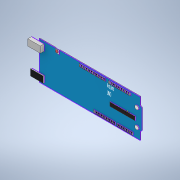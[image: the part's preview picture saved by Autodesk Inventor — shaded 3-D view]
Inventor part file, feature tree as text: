
AUTODESK INVENTOR PART (.ipt)
format: ipt  version: 2021 (Build 250183000, 183)  size: 493,056 bytes
history: native  units: mm
features: sketch x8, extrude x8
ambient origin geometry x8: Origin, YZ Plane, XZ Plane, XY Plane, X Axis, Y Axis, Z Axis, Center Point
bodies: Solid1 (feature_tree)
feature tree (16):
  sketch  "Sketch1"  dims[d0=30.0mm d1=80.0mm]
  extrude  "Extrusion1"  Depth=80.0mm
  extrude  "Extrusion2"  Depth=3.0mm
  extrude  "Extrusion3"  Depth=3.0mm TaperAngle=0.0deg
  extrude  "Extrusion4"  Depth=0.5mm TaperAngle=0.0deg
  extrude  "Extrusion8"  Depth=0.2mm TaperAngle=0.0deg
  extrude  "Extrusion9"  Depth=10.0mm
  sketch  "Sketch2"  dims[d17=100.0mm d19=10.0mm d21=100.0mm d23=10.0mm d32=100.0mm d34=10.0mm d42=100.0mm d44=10.0mm d46=80.0mm d48=10.0mm d50=80.0mm d52=10.0mm d53=1.0mm d54=10.0mm d56=100.0mm d58=10.0mm d60=80.0mm d62=10.0mm d64=80.0mm d66=10.0mm d68=80.0mm d70=10.0mm d72=100.0mm d74=10.0mm d76=80.0mm d78=10.0mm d80=80.0mm d82=10.0mm d84=80.0mm d86=10.0mm d87=3.0mm]
  sketch  "Sketch3"  dims[d88=3.0mm d89=3.0mm d90=0.0mm]
  sketch  "Sketch4"  dims[d91=1.0mm d92=0.0mm d93=0.5mm d94=0.0mm]
  sketch  "Sketch5"  dims[d95=0.5mm d96=0.0mm d103=0.2mm d104=0.0mm]
  sketch  "Sketch6"  dims[d105=0.5mm d106=0.0mm d107=10.0mm]
  sketch  "Sketch7"  dims[d108=5.0mm d109=10.0mm]
  sketch  "Sketch8"  dims[d110=5.0mm d113=20.0mm d114=3.0mm d115=3.0mm d116=3.0mm d117=2.0mm d122=17.0mm d123=2.0mm d124=20.5mm d125=2.0mm d126=17.0mm d127=2.0mm d128=12.5mm d129=2.0mm d130=17.0mm d131=2.0mm d132=1.5mm d133=1.5mm d134=100.0mm d136=2.0mm d137=10.0mm d139=10.0mm d142=100.0mm d144=10.0mm d145=1.5mm d146=1.5mm d148=100.0mm d150=10.0mm d151=1.5mm d152=1.5mm d154=100.0mm d156=10.0mm d157=1.5mm d158=1.5mm d159=80.0mm d161=2.0mm d162=10.0mm d164=10.0mm d166=80.0mm d168=2.0mm d169=10.0mm d171=10.0mm d173=60.0mm d175=2.0mm d176=10.0mm d178=10.0mm d180=0.1mm d181=0.0mm d182=0.5mm d183=0.0mm]
  extrude  "Extrusion10"  Depth=10.0mm
  extrude  "Extrusion11"  Depth=20.0mm
